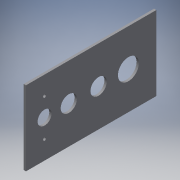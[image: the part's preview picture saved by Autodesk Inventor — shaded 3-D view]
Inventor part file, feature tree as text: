
AUTODESK INVENTOR PART (.ipt)
format: ipt  version: 2018 (Build 220112000, 112)  size: 153,600 bytes
history: native  units: in
note: dims shown in document units (in); Inventor stores cm internally (conversion verified against a paired STEP export)
features: extrude x4, sketch x4
ambient origin geometry x8: Origin, YZ Plane, XZ Plane, XY Plane, X Axis, Y Axis, Z Axis, Center Point
bodies: Solid1 (feature_tree)
feature tree (8):
  extrude  "Extrusion1"  Depth=7.0in
  extrude  "Extrusion2"  Depth=0.125in
  extrude  "Extrusion3"  Depth=0.875in
  extrude  "Extrusion4"  Depth=1.6in
  sketch  "Sketch1"  dims[d0=4.0in d1=7.0in]
  sketch  "Sketch2"  dims[d2=0.125in d3=0.0in d4=1.0in]
  sketch  "Sketch3"  dims[d5=1.3in d7=0.875in]
  sketch  "Sketch4"  dims[d8=1.6in d9=1.6in d10=0.875in d11=1.125in d12=0.5in d13=0.0in d14=0.75in d17=0.159in d18=0.159in d19=1.0in d20=0.0in d23=1.0in d24=0.5in d25=0.5in d26=0.5in d27=0.5in d28=0.5in d29=0.5in d30=0.5in d31=0.5in d32=0.2in d33=0.2in d34=0.2in d35=0.2in d36=1.0in d37=0.0in]
